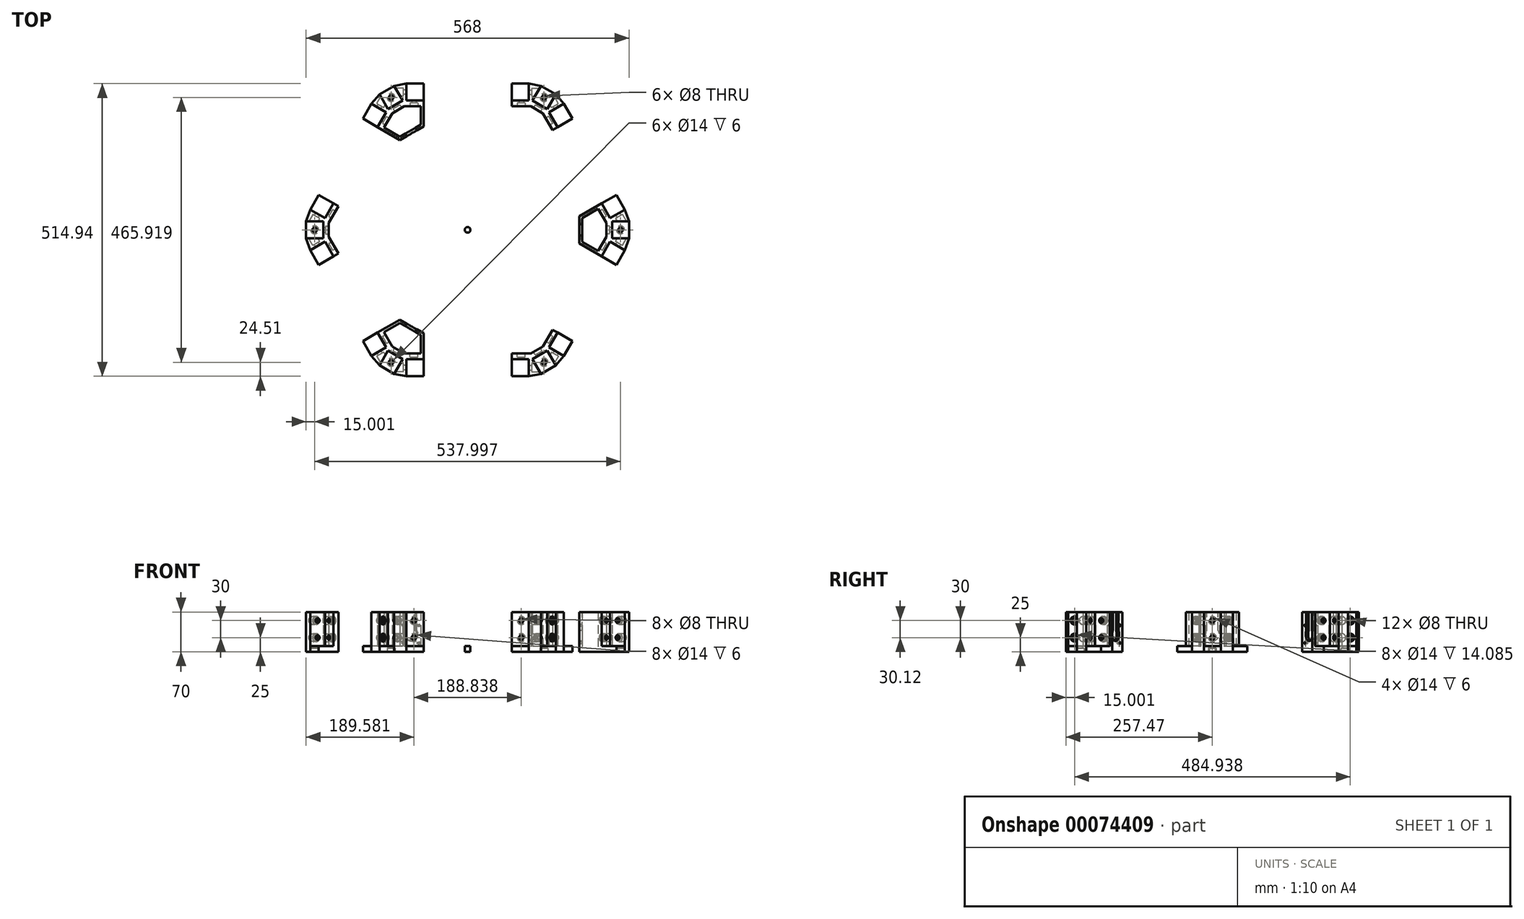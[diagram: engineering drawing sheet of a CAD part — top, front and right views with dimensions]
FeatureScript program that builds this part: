
annotation { "Feature Type Name" : "Feature", "Feature Type Description" : "" }
export const myFeature = defineFeature(function(context is Context, id is Id, definition is map)
    precondition{}
    {
        {
            var Q0;
            Q0=qCreatedBy(makeId("Top.planeOp"),FACE);
            var sketch = newSketch(context, id + "F0", { "sketchPlane" : qUnion([Q0])});
            skCircle(sketch, "E0", {"center": v(0, 0) * mm, "radius": 150 * mm, "construction": true});
            skCircle(sketch, "E1.cCircle", {"center": v(0, 0) * mm, "radius": 253.45 * mm, "construction": true});
            skLineSegment(sketch, "E1.0", {"start": v(-146.33, 253.45) * mm, "end": v(146.33, 253.45) * mm, "construction": true});
            skLineSegment(sketch, "E1.1", {"start": v(146.33, 253.45) * mm, "end": v(292.66, 0) * mm, "construction": true});
            skLineSegment(sketch, "E1.2", {"start": v(292.66, 0) * mm, "end": v(146.33, -253.45) * mm, "construction": true});
            skLineSegment(sketch, "E1.3", {"start": v(146.33, -253.45) * mm, "end": v(-146.33, -253.45) * mm, "construction": true});
            skLineSegment(sketch, "E1.4", {"start": v(-146.33, -253.45) * mm, "end": v(-292.66, 0) * mm, "construction": true});
            skLineSegment(sketch, "E1.5", {"start": v(-292.66, 0) * mm, "end": v(-146.33, 253.45) * mm, "construction": true});
            skPoint(sketch, "E1.0.midPoint", {"position": v(0, 253.45) * mm});
            skLineSegment(sketch, "E2", {"start": v(146.33, 253.45) * mm, "end": v(-146.33, -253.45) * mm, "construction": true});
            skCircle(sketch, "E3.cCircle", {"center": v(0, 0) * mm, "radius": 284 * mm, "construction": true});
            skLineSegment(sketch, "E3.0", {"start": v(0, 327.93) * mm, "end": v(284, 163.97) * mm, "construction": true});
            skLineSegment(sketch, "E3.1", {"start": v(284, 163.97) * mm, "end": v(284, -163.97) * mm, "construction": true});
            skLineSegment(sketch, "E3.2", {"start": v(284, -163.97) * mm, "end": v(0, -327.93) * mm, "construction": true});
            skLineSegment(sketch, "E3.3", {"start": v(0, -327.93) * mm, "end": v(-284, -163.97) * mm, "construction": true});
            skLineSegment(sketch, "E3.4", {"start": v(-284, -163.97) * mm, "end": v(-284, 163.97) * mm, "construction": true});
            skLineSegment(sketch, "E3.5", {"start": v(-284, 163.97) * mm, "end": v(0, 327.93) * mm, "construction": true});
            skPoint(sketch, "E3.0.midPoint", {"position": v(142, 245.95) * mm});
            skLineSegment(sketch, "E4", {"start": v(154.99, 238.45) * mm, "end": v(129, 253.45) * mm});
            skLineSegment(sketch, "E5", {"start": v(-154.99, 238.45) * mm, "end": v(-129, 253.45) * mm});
            skLineSegment(sketch, "E6", {"start": v(-129, 253.45) * mm, "end": v(-114, 227.47) * mm});
            skLineSegment(sketch, "E7", {"start": v(-114, 227.47) * mm, "end": v(-139.99, 212.47) * mm});
            skLineSegment(sketch, "E8", {"start": v(-139.99, 212.47) * mm, "end": v(-154.99, 238.45) * mm});
            skLineSegment(sketch, "E9", {"start": v(129, 253.45) * mm, "end": v(114, 227.47) * mm});
            skLineSegment(sketch, "E10", {"start": v(114, 227.47) * mm, "end": v(139.99, 212.47) * mm});
            skLineSegment(sketch, "E11", {"start": v(139.99, 212.47) * mm, "end": v(154.99, 238.45) * mm});
            skLineSegment(sketch, "E12", {"start": v(284, 15) * mm, "end": v(284, -15) * mm});
            skLineSegment(sketch, "E13", {"start": v(284, -15) * mm, "end": v(254, -15) * mm});
            skLineSegment(sketch, "E14", {"start": v(254, -15) * mm, "end": v(254, 15) * mm});
            skLineSegment(sketch, "E15", {"start": v(254, 15) * mm, "end": v(284, 15) * mm});
            skLineSegment(sketch, "E16", {"start": v(154.99, -238.45) * mm, "end": v(129, -253.45) * mm});
            skLineSegment(sketch, "E17", {"start": v(129, -253.45) * mm, "end": v(114, -227.47) * mm});
            skLineSegment(sketch, "E18", {"start": v(114, -227.47) * mm, "end": v(139.99, -212.47) * mm});
            skLineSegment(sketch, "E19", {"start": v(139.99, -212.47) * mm, "end": v(154.99, -238.45) * mm});
            skLineSegment(sketch, "E20", {"start": v(-129, -253.45) * mm, "end": v(-154.99, -238.45) * mm});
            skLineSegment(sketch, "E21", {"start": v(-154.99, -238.45) * mm, "end": v(-139.99, -212.47) * mm});
            skLineSegment(sketch, "E22", {"start": v(-139.99, -212.47) * mm, "end": v(-114, -227.47) * mm});
            skLineSegment(sketch, "E23", {"start": v(-114, -227.47) * mm, "end": v(-129, -253.45) * mm});
            skLineSegment(sketch, "E24", {"start": v(-284, -15) * mm, "end": v(-284, 15) * mm});
            skLineSegment(sketch, "E25", {"start": v(-284, 15) * mm, "end": v(-254, 15) * mm});
            skLineSegment(sketch, "E26", {"start": v(-254, 15) * mm, "end": v(-254, -15) * mm});
            skLineSegment(sketch, "E27", {"start": v(-254, -15) * mm, "end": v(-284, -15) * mm});
            skLineSegment(sketch, "E28", {"start": v(-254, 15) * mm, "end": v(-139.99, 212.47) * mm, "construction": true});
            skLineSegment(sketch, "E29", {"start": v(-254, -15) * mm, "end": v(-139.99, -212.47) * mm, "construction": true});
            skLineSegment(sketch, "E30", {"start": v(-114, -227.47) * mm, "end": v(114, -227.47) * mm, "construction": true});
            skLineSegment(sketch, "E31", {"start": v(139.99, -212.47) * mm, "end": v(254, -15) * mm, "construction": true});
            skLineSegment(sketch, "E32", {"start": v(254, 15) * mm, "end": v(139.99, 212.47) * mm, "construction": true});
            skLineSegment(sketch, "E33", {"start": v(114, 227.47) * mm, "end": v(-114, 227.47) * mm, "construction": true});
            skLineSegment(sketch, "E34", {"start": v(-114, 227.47) * mm, "end": v(-107.5, 227.47) * mm, "construction": true});
            skLineSegment(sketch, "E35", {"start": v(-107.5, 227.47) * mm, "end": v(-77.5, 227.47) * mm});
            skLineSegment(sketch, "E36", {"start": v(-77.5, 227.47) * mm, "end": v(-77.5, 217.47) * mm});
            skLineSegment(sketch, "E37", {"start": v(-77.5, 217.47) * mm, "end": v(-111.33, 217.47) * mm});
            skLineSegment(sketch, "E38", {"start": v(-111.33, 217.47) * mm, "end": v(-132.67, 205.15) * mm});
            skLineSegment(sketch, "E39", {"start": v(-132.67, 205.15) * mm, "end": v(-149.58, 175.86) * mm});
            skLineSegment(sketch, "E40", {"start": v(-149.58, 175.86) * mm, "end": v(-158.24, 180.86) * mm});
            skLineSegment(sketch, "E41", {"start": v(-158.24, 180.86) * mm, "end": v(-143.24, 206.84) * mm});
            skLineSegment(sketch, "E42", {"start": v(-143.24, 206.84) * mm, "end": v(-139.99, 212.47) * mm, "construction": true});
            skLineSegment(sketch, "E43", {"start": v(-154.99, 238.45) * mm, "end": v(-114, 227.47) * mm, "construction": true});
            skLineSegment(sketch, "E44", {"start": v(-129, 253.45) * mm, "end": v(-139.99, 212.47) * mm, "construction": true});
            skPoint(sketch, "E45", {"position": v(-134.5, 232.96) * mm});
            skCircle(sketch, "E46", {"center": v(0, 0) * mm, "radius": 5 * mm});
            skLineSegment(sketch, "E47", {"start": v(-118.15, 234.63) * mm, "end": v(-118.15, 248.63) * mm, "construction": true});
            skLineSegment(sketch, "E48.0", {"start": v(-112.15, 234.63) * mm, "end": v(-112.15, 248.63) * mm, "construction": true});
            skLineSegment(sketch, "E49.0", {"start": v(-107.5, 257.47) * mm, "end": v(-77.5, 257.47) * mm});
            skLineSegment(sketch, "E50.0", {"start": v(-184.22, 195.86) * mm, "end": v(-169.22, 221.84) * mm});
            skLineSegment(sketch, "E51", {"start": v(-154.99, 238.45) * mm, "end": v(-169.22, 221.84) * mm});
            skLineSegment(sketch, "E52", {"start": v(-107.5, 257.47) * mm, "end": v(-129, 253.45) * mm});
            skLineSegment(sketch, "E53", {"start": v(-107.5, 227.47) * mm, "end": v(-107.5, 257.47) * mm});
            skLineSegment(sketch, "E54", {"start": v(-77.5, 257.47) * mm, "end": v(-77.5, 227.47) * mm});
            skLineSegment(sketch, "E55", {"start": v(-158.24, 180.86) * mm, "end": v(-184.22, 195.86) * mm});
            skLineSegment(sketch, "E56", {"start": v(-143.24, 206.84) * mm, "end": v(-169.22, 221.84) * mm});
            skLineSegment(sketch, "E57", {"start": v(-107.5, 242.47) * mm, "end": v(-122.67, 242.47) * mm, "construction": true});
            skLineSegment(sketch, "E58", {"start": v(-149.58, 175.86) * mm, "end": v(-118.88, 158.14) * mm});
            skLineSegment(sketch, "E59", {"start": v(-118.88, 158.14) * mm, "end": v(-77.5, 182.02) * mm});
            skLineSegment(sketch, "E60", {"start": v(-77.5, 182.02) * mm, "end": v(-77.5, 217.47) * mm});
            skLineSegment(sketch, "E61", {"start": v(-122, 211.3) * mm, "end": v(-98.2, 170.08) * mm, "construction": true});
            skLineSegment(sketch, "E62.1", {"start": v(-118.88, 163.9) * mm, "end": v(-82.5, 184.9) * mm});
            skLineSegment(sketch, "E62.2", {"start": v(-147.08, 180.19) * mm, "end": v(-118.88, 163.9) * mm});
            skLineSegment(sketch, "E63", {"start": v(-82.5, 184.9) * mm, "end": v(-82.5, 217.47) * mm});
            skSolve(sketch);
        }
        {
            var Q0;
            Q0=makeQuery(id+"F0.imprint","IMPRINT",FACE,{"disambiguationData":[TD([[makeQuery(id+"F0.imprint","IMPRINT",EDGE,{"derivedFrom":sQuery(id+"F0.wireOp",EDGE,"E6")}),1.0]])]});
            var Q1;
            Q1=makeQuery(id+"F0.imprint","IMPRINT",FACE,{"disambiguationData":[TD([[makeQuery(id+"F0.imprint","IMPRINT",EDGE,{"derivedFrom":sQuery(id+"F0.wireOp",EDGE,"E25")}),1.0]])]});
            extrude(context, id + "F1", {"entities" : qUnion([Q0, Q1]), "depth" : 70 * mm});
        }
        {
            var Q0;
            Q0=makeQuery(id+"F0.imprint","IMPRINT",FACE,{"disambiguationData":[TD([[makeQuery(id+"F0.imprint","IMPRINT",EDGE,{"derivedFrom":sQuery(id+"F0.wireOp",EDGE,"gfhvg1Dc-7iLy-Ra7s-P4iO-IVNU9nK08UEl")}),-1.0]])]});
            var Q1;
            Q1=makeQuery(id+"F0.imprint","IMPRINT",FACE,{"disambiguationData":[TD([[makeQuery(id+"F0.imprint","IMPRINT",EDGE,{"derivedFrom":sQuery(id+"F0.wireOp",EDGE,"E5")}),-1.0]])]});
            var Q2;
            Q2=makeQuery(id+"F0.imprint","IMPRINT",FACE,{"disambiguationData":[TD([[makeQuery(id+"F0.imprint","IMPRINT",EDGE,{"derivedFrom":sQuery(id+"F0.wireOp",EDGE,"E41")}),1.0]])]});
            var Q3;
            Q3=makeQuery(id+"F0.imprint","IMPRINT",FACE,{"disambiguationData":[TD([[makeQuery(id+"F0.imprint","IMPRINT",EDGE,{"derivedFrom":sQuery(id+"F0.wireOp",EDGE,"kg992uxK-LLUE-ufWO-S31q-0ohrqG9XmHnS")}),1.0]])]});
            var Q4;
            Q4=makeQuery(id+"F0.imprint","IMPRINT",FACE,{"disambiguationData":[TD([[makeQuery(id+"F0.imprint","IMPRINT",EDGE,{"derivedFrom":sQuery(id+"F0.wireOp",EDGE,"zyB05oXD-GM3K-m8Ih-r1cb-nkl0ugIBj9Wl")}),1.0]])]});
            var Q5;
            Q5=makeQuery(id+"F0.imprint","IMPRINT",FACE,{"disambiguationData":[TD([[makeQuery(id+"F0.imprint","IMPRINT",EDGE,{"derivedFrom":sQuery(id+"F0.wireOp",EDGE,"ZcA5kg2R-B5n5-RwAf-hmlT-K68Li3uCES3B")}),-1.0]])]});
            var Q6;
            Q6=makeQuery(id+"F0.imprint","IMPRINT",FACE,{"disambiguationData":[TD([[makeQuery(id+"F0.imprint","IMPRINT",EDGE,{"derivedFrom":sQuery(id+"F0.wireOp",EDGE,"E46")}),1.0]])]});
            var Q7;
            Q7=makeQuery(id+"F0.imprint","IMPRINT",FACE,{"disambiguationData":[TD([[makeQuery(id+"F0.imprint","IMPRINT",EDGE,{"derivedFrom":sQuery(id+"F0.wireOp",EDGE,"E35")}),1.0]])]});
            extrude(context, id + "F2", {"entities" : qUnion([Q0, Q1, Q2, Q3, Q4, Q5, Q6, Q7]), "operationType" : NewBodyOperationType.ADD, "depth" : 10 * mm});
        }
        {
            var Q0;
            Q0=makeQuery(id+"F1.opExtrude","SWEPT_FACE",FACE,{"disambiguationData":[OSD([sQuery(id+"F0.wireOp",EDGE,"E53")])]});
            var Q1;
            Q1=makeQuery(id+"F1.opExtrude","CAP_VERTEX",VERTEX,{"disambiguationData":[OSD([sQuery(id+"F0.wireOp",EDGE,"E5"),sQuery(id+"F0.wireOp",EDGE,"E6"),sQuery(id+"F0.wireOp",EDGE,"E52")])],"isStart":false});
            cPlane(context, id + "F3", {"entities" : qUnion([Q0, Q1]), "cplaneType" : CPlaneType.PLANE_POINT, "offset" : 150 * mm, "width" : 150 * mm, "height" : 150 * mm});
        }
        {
            var Q0;
            Q0=qCreatedBy(id+"F3.planeOp",FACE);
            var sketch = newSketch(context, id + "F4", { "sketchPlane" : qUnion([Q0])});
            skLineSegment(sketch, "E64.0", {"start": v(242.47, 70.12) * mm, "end": v(242.47, 10) * mm, "construction": true});
            skPoint(sketch, "E65", {"position": v(242.47, 55.12) * mm});
            skPoint(sketch, "E66", {"position": v(242.47, 25) * mm});
            skSolve(sketch);
        }
        {
            var Q0;
            Q0=makeQuery(id+"F1.opExtrude","SWEPT_FACE",FACE,{"disambiguationData":[OSD([sQuery(id+"F0.wireOp",EDGE,"E56")])]});
            var Q1;
            Q1=makeQuery(id+"F1.opExtrude","CAP_VERTEX",VERTEX,{"disambiguationData":[OSD([sQuery(id+"F0.wireOp",EDGE,"E5"),sQuery(id+"F0.wireOp",EDGE,"E8"),sQuery(id+"F0.wireOp",EDGE,"E51")])],"isStart":false});
            cPlane(context, id + "F5", {"entities" : qUnion([Q0, Q1]), "cplaneType" : CPlaneType.PLANE_POINT, "offset" : 150 * mm, "width" : 150 * mm, "height" : 150 * mm});
        }
        {
            var Q0;
            Q0=qCreatedBy(id+"F5.planeOp",FACE);
            var sketch = newSketch(context, id + "F6", { "sketchPlane" : qUnion([Q0])});
            skLineSegment(sketch, "E67.0", {"start": v(-242.47, 70) * mm, "end": v(-242.47, 10) * mm, "construction": true});
            skPoint(sketch, "E68", {"position": v(-242.47, 55) * mm});
            skPoint(sketch, "E69", {"position": v(-242.47, 25) * mm});
            skSolve(sketch);
        }
        {
            var Q0;
            Q0=makeQuery(id+"F1.opExtrude","SWEPT_FACE",FACE,{"disambiguationData":[OSD([sQuery(id+"F0.wireOp",EDGE,"E38")])]});
            var sketch = newSketch(context, id + "F7", { "sketchPlane" : qUnion([Q0])});
            skLineSegment(sketch, "E70", {"start": v(0, 70) * mm, "end": v(0, 0) * mm, "construction": true});
            skPoint(sketch, "E71", {"position": v(0, 55) * mm});
            skPoint(sketch, "E72", {"position": v(0, 25) * mm});
            skSolve(sketch);
        }
        {
            var Q0;
            Q0=makeQuery(id+"F1.opExtrude","SWEPT_FACE",FACE,{"disambiguationData":[OSD([sQuery(id+"F0.wireOp",EDGE,"E39")])]});
            var sketch = newSketch(context, id + "F8", { "sketchPlane" : qUnion([Q0])});
            skLineSegment(sketch, "E73", {"start": v(94.42, 70) * mm, "end": v(94.42, 0) * mm, "construction": true});
            skPoint(sketch, "E74", {"position": v(94.42, 55) * mm});
            skPoint(sketch, "E75", {"position": v(94.42, 25) * mm});
            skSolve(sketch);
        }
        {
            var Q0;
            Q0=makeQuery(id+"F1.opExtrude","SWEPT_FACE",FACE,{"disambiguationData":[OSD([sQuery(id+"F0.wireOp",EDGE,"E37")])]});
            var sketch = newSketch(context, id + "F9", { "sketchPlane" : qUnion([Q0])});
            skLineSegment(sketch, "E76", {"start": v(-94.42, 70) * mm, "end": v(-94.42, 0) * mm, "construction": true});
            skPoint(sketch, "E77", {"position": v(-94.42, 55) * mm});
            skPoint(sketch, "E78", {"position": v(-94.42, 25) * mm});
            skSolve(sketch);
        }
        {
            var Q0;
            Q0=sQuery(id+"F4.wireOp",VERTEX,"E65");
            var Q1;
            Q1=sQuery(id+"F4.wireOp",VERTEX,"E66");
            var Q2;
            Q2=sQuery(id+"F0.wireOp",VERTEX,"E45");
            var Q3;
            Q3=sQuery(id+"F6.wireOp",VERTEX,"cff155ce-5f81-47e9-b263-279717c5aa05");
            var Q4;
            Q4=sQuery(id+"F6.wireOp",VERTEX,"238236e4-252f-4cb6-8429-7a6d3b7dbdbb");
            var Q5;
            Q5=sQuery(id+"F6.wireOp",VERTEX,"E68");
            var Q6;
            Q6=sQuery(id+"F6.wireOp",VERTEX,"E69");
            var Q7;
            Q7=makeQuery(id+"F1.opExtrude","SWEPT_BODY",BODY,{"disambiguationData":[OSD([sQuery(id+"F0.wireOp",EDGE,"E6"),sQuery(id+"F0.wireOp",EDGE,"E7"),sQuery(id+"F0.wireOp",EDGE,"E8"),sQuery(id+"F0.wireOp",EDGE,"gfhvg1Dc-7iLy-Ra7s-P4iO-IVNU9nK08UEl"),sQuery(id+"F0.wireOp",EDGE,"2Ei9XriT-fD9c-ETMH-U4qR-QOi2l2HyO4ls"),sQuery(id+"F0.wireOp",EDGE,"E35"),sQuery(id+"F0.wireOp",EDGE,"E36"),sQuery(id+"F0.wireOp",EDGE,"E37"),sQuery(id+"F0.wireOp",EDGE,"E38"),sQuery(id+"F0.wireOp",EDGE,"E39"),sQuery(id+"F0.wireOp",EDGE,"E40"),sQuery(id+"F0.wireOp",EDGE,"E41"),sQuery(id+"F0.wireOp",EDGE,"uSjWHJkC-35aW-f7bu-jVbw-ONZoDCyZtA0Y"),sQuery(id+"F0.wireOp",EDGE,"6PwrACHb-G9Z9-2ubd-gtxy-jkFo4IrFMrrZ")])]});
            hole(context, id + "F10", {"style" : HoleStyle.C_BORE, "holeDiameter" : 8 * mm, "cBoreDiameter" : 14 * mm, "cBoreDepth" : 6 * mm, "endStyle" : HoleEndStyle.BLIND, "oppositeDirection" : true, "holeDepth" : 20 * mm, "locations" : qUnion([Q0, Q1, Q2, Q3, Q4, Q5, Q6]), "scope" : qUnion([Q7])});
        }
        {
            var Q0;
            Q0=sQuery(id+"F9.wireOp",VERTEX,"E77");
            var Q1;
            Q1=sQuery(id+"F9.wireOp",VERTEX,"E78");
            var Q2;
            Q2=sQuery(id+"F7.wireOp",VERTEX,"E71");
            var Q3;
            Q3=sQuery(id+"F7.wireOp",VERTEX,"E72");
            var Q4;
            Q4=sQuery(id+"F8.wireOp",VERTEX,"E75");
            var Q5;
            Q5=sQuery(id+"F8.wireOp",VERTEX,"E74");
            var Q6;
            Q6=makeQuery(id+"F1.opExtrude","SWEPT_BODY",BODY,{"disambiguationData":[OSD([sQuery(id+"F0.wireOp",EDGE,"E6"),sQuery(id+"F0.wireOp",EDGE,"E7"),sQuery(id+"F0.wireOp",EDGE,"E8"),sQuery(id+"F0.wireOp",EDGE,"gfhvg1Dc-7iLy-Ra7s-P4iO-IVNU9nK08UEl"),sQuery(id+"F0.wireOp",EDGE,"2Ei9XriT-fD9c-ETMH-U4qR-QOi2l2HyO4ls"),sQuery(id+"F0.wireOp",EDGE,"E35"),sQuery(id+"F0.wireOp",EDGE,"E36"),sQuery(id+"F0.wireOp",EDGE,"E37"),sQuery(id+"F0.wireOp",EDGE,"E38"),sQuery(id+"F0.wireOp",EDGE,"E39"),sQuery(id+"F0.wireOp",EDGE,"E40"),sQuery(id+"F0.wireOp",EDGE,"E41"),sQuery(id+"F0.wireOp",EDGE,"uSjWHJkC-35aW-f7bu-jVbw-ONZoDCyZtA0Y"),sQuery(id+"F0.wireOp",EDGE,"6PwrACHb-G9Z9-2ubd-gtxy-jkFo4IrFMrrZ")])]});
            hole(context, id + "F11", {"style" : HoleStyle.C_BORE, "holeDiameter" : 8 * mm, "cBoreDiameter" : 14 * mm, "cBoreDepth" : 6 * mm, "endStyle" : HoleEndStyle.THROUGH, "locations" : qUnion([Q0, Q1, Q2, Q3, Q4, Q5]), "scope" : qUnion([Q6])});
        }
        {
            var Q0;
            Q0=makeQuery(id+"F1.opExtrude","SWEPT_BODY",BODY,{"disambiguationData":[OSD([sQuery(id+"F0.wireOp",EDGE,"E6"),sQuery(id+"F0.wireOp",EDGE,"E7"),sQuery(id+"F0.wireOp",EDGE,"E8"),sQuery(id+"F0.wireOp",EDGE,"gfhvg1Dc-7iLy-Ra7s-P4iO-IVNU9nK08UEl"),sQuery(id+"F0.wireOp",EDGE,"2Ei9XriT-fD9c-ETMH-U4qR-QOi2l2HyO4ls"),sQuery(id+"F0.wireOp",EDGE,"E35"),sQuery(id+"F0.wireOp",EDGE,"E36"),sQuery(id+"F0.wireOp",EDGE,"E37"),sQuery(id+"F0.wireOp",EDGE,"E38"),sQuery(id+"F0.wireOp",EDGE,"E39"),sQuery(id+"F0.wireOp",EDGE,"E40"),sQuery(id+"F0.wireOp",EDGE,"E41"),sQuery(id+"F0.wireOp",EDGE,"uSjWHJkC-35aW-f7bu-jVbw-ONZoDCyZtA0Y"),sQuery(id+"F0.wireOp",EDGE,"6PwrACHb-G9Z9-2ubd-gtxy-jkFo4IrFMrrZ")])]});
            var Q1;
            Q1=sQuery(id+"F0.wireOp",EDGE,"E3.cCircle");
            circularPattern(context, id + "F12", {"entities" : qUnion([Q0]), "axis" : qUnion([Q1]), "angle" : 60 * degree, "instanceCount" : 2});
        }
        {
            var Q0;
            {var subQ0=sQuery(id+"F0.wireOp",EDGE,"E58");Q0=makeQuery(id+"F0.imprint","IMPRINT",FACE,{"disambiguationData":[TD([[makeQuery(id+"F0.imprint","IMPRINT",EDGE,{"derivedFrom":subQ0}),1.0]])]});}
            extrude(context, id + "F13", {"entities" : qUnion([Q0]), "operationType" : NewBodyOperationType.ADD, "depth" : 70 * mm});
        }
        {
            var Q0;
            Q0=makeQuery(id+"F13.opExtrude","SWEPT_FACE",FACE,{"disambiguationData":[OSD([sQuery(id+"F0.wireOp",EDGE,"E59")])]});
            var sketch = newSketch(context, id + "F14", { "sketchPlane" : qUnion([Q0])});
            skLineSegment(sketch, "E79.0", {"start": v(-23.89, 10) * mm, "end": v(23.89, 10) * mm, "construction": true});
            skLineSegment(sketch, "E80.0", {"start": v(-23.89, 52) * mm, "end": v(23.89, 52) * mm, "construction": true});
            skLineSegment(sketch, "E81.0", {"start": v(-23.89, 46.5) * mm, "end": v(23.89, 46.5) * mm, "construction": true});
            skLineSegment(sketch, "E82.0", {"start": v(-23.89, 15.5) * mm, "end": v(23.89, 15.5) * mm, "construction": true});
            skPoint(sketch, "E83", {"position": v(0, 31) * mm});
            skLineSegment(sketch, "E84", {"start": v(0, 70) * mm, "end": v(0, 0) * mm, "construction": true});
            skLineSegment(sketch, "E85.0", {"start": v(-15.5, 70) * mm, "end": v(-15.5, 0) * mm, "construction": true});
            skLineSegment(sketch, "E86.0", {"start": v(15.5, 70) * mm, "end": v(15.5, 0) * mm, "construction": true});
            skLineSegment(sketch, "E87", {"start": v(15.5, 15.5) * mm, "end": v(-15.5, 46.5) * mm, "construction": true});
            skLineSegment(sketch, "E88", {"start": v(15.5, 46.5) * mm, "end": v(-15.5, 15.5) * mm, "construction": true});
            skCircle(sketch, "E89", {"center": v(0, 31) * mm, "radius": 12 * mm});
            skLineSegment(sketch, "E90.0", {"start": v(-10, 70) * mm, "end": v(-10, 0) * mm, "construction": true});
            skLineSegment(sketch, "E91.0", {"start": v(10, 70) * mm, "end": v(10, 0) * mm, "construction": true});
            skLineSegment(sketch, "E92", {"start": v(-10, 37.63) * mm, "end": v(-10, 70) * mm});
            skLineSegment(sketch, "E93", {"start": v(10, 37.63) * mm, "end": v(10, 70) * mm});
            skSolve(sketch);
        }
        {
            var Q0;
            Q0 = qSketchRegion(id + "F14", true);
            var Q1;
            {var subQ0=sQuery(id+"F14.wireOp",EDGE,"E92");Q1=makeQuery(id+"F14.imprint","IMPRINT",FACE,{"disambiguationData":[TD([[makeQuery(id+"F14.imprint","IMPRINT",EDGE,{"derivedFrom":subQ0}),-1.0]])]});}
            extrude(context, id + "F15", {"entities" : qUnion([Q0, Q1]), "operationType" : NewBodyOperationType.REMOVE, "oppositeDirection" : true, "depth" : 5 * mm});
        }
        {
            var Q0;
            Q0=sQuery(id+"F14.wireOp",VERTEX,"E87.end");
            var Q1;
            Q1=sQuery(id+"F14.wireOp",VERTEX,"E88.start");
            var Q2;
            Q2=sQuery(id+"F14.wireOp",VERTEX,"E87.start");
            var Q3;
            Q3=sQuery(id+"F14.wireOp",VERTEX,"E88.end");
            var Q4;
            Q4=makeQuery(id+"F1.opExtrude","SWEPT_BODY",BODY,{"disambiguationData":[OSD([sQuery(id+"F0.wireOp",EDGE,"E6"),sQuery(id+"F0.wireOp",EDGE,"E7"),sQuery(id+"F0.wireOp",EDGE,"E8"),sQuery(id+"F0.wireOp",EDGE,"E35"),sQuery(id+"F0.wireOp",EDGE,"E36"),sQuery(id+"F0.wireOp",EDGE,"E37"),sQuery(id+"F0.wireOp",EDGE,"E38"),sQuery(id+"F0.wireOp",EDGE,"E39"),sQuery(id+"F0.wireOp",EDGE,"E40"),sQuery(id+"F0.wireOp",EDGE,"E41"),sQuery(id+"F0.wireOp",EDGE,"E51"),sQuery(id+"F0.wireOp",EDGE,"E52"),sQuery(id+"F0.wireOp",EDGE,"E53"),sQuery(id+"F0.wireOp",EDGE,"E56")])]});
            hole(context, id + "F16", {"style" : HoleStyle.SIMPLE, "holeDiameter" : 3 * mm, "endStyle" : HoleEndStyle.BLIND, "holeDepth" : 20 * mm, "locations" : qUnion([Q0, Q1, Q2, Q3]), "scope" : qUnion([Q4])});
        }
        {
            var Q0;
            Q0=makeQuery(id+"F1.opExtrude","SWEPT_BODY",BODY,{"disambiguationData":[OSD([sQuery(id+"F0.wireOp",EDGE,"E6"),sQuery(id+"F0.wireOp",EDGE,"E7"),sQuery(id+"F0.wireOp",EDGE,"E8"),sQuery(id+"F0.wireOp",EDGE,"gfhvg1Dc-7iLy-Ra7s-P4iO-IVNU9nK08UEl"),sQuery(id+"F0.wireOp",EDGE,"2Ei9XriT-fD9c-ETMH-U4qR-QOi2l2HyO4ls"),sQuery(id+"F0.wireOp",EDGE,"E35"),sQuery(id+"F0.wireOp",EDGE,"E36"),sQuery(id+"F0.wireOp",EDGE,"E37"),sQuery(id+"F0.wireOp",EDGE,"E38"),sQuery(id+"F0.wireOp",EDGE,"E39"),sQuery(id+"F0.wireOp",EDGE,"E40"),sQuery(id+"F0.wireOp",EDGE,"E41"),sQuery(id+"F0.wireOp",EDGE,"uSjWHJkC-35aW-f7bu-jVbw-ONZoDCyZtA0Y"),sQuery(id+"F0.wireOp",EDGE,"6PwrACHb-G9Z9-2ubd-gtxy-jkFo4IrFMrrZ")])]});
            var Q1;
            Q1=sQuery(id+"F0.wireOp",EDGE,"E3.cCircle");
            circularPattern(context, id + "F17", {"entities" : qUnion([Q0]), "axis" : qUnion([Q1]), "angle" : 120 * degree, "instanceCount" : 3});
        }
        {
            var Q0;
            Q0=makeQuery(id+"F12.opPattern","COPY",BODY,{"derivedFrom":makeQuery(id+"F1.opExtrude","SWEPT_BODY",BODY,{"disambiguationData":[OSD([sQuery(id+"F0.wireOp",EDGE,"E6"),sQuery(id+"F0.wireOp",EDGE,"E7"),sQuery(id+"F0.wireOp",EDGE,"E8"),sQuery(id+"F0.wireOp",EDGE,"gfhvg1Dc-7iLy-Ra7s-P4iO-IVNU9nK08UEl"),sQuery(id+"F0.wireOp",EDGE,"2Ei9XriT-fD9c-ETMH-U4qR-QOi2l2HyO4ls"),sQuery(id+"F0.wireOp",EDGE,"E35"),sQuery(id+"F0.wireOp",EDGE,"E36"),sQuery(id+"F0.wireOp",EDGE,"E37"),sQuery(id+"F0.wireOp",EDGE,"E38"),sQuery(id+"F0.wireOp",EDGE,"E39"),sQuery(id+"F0.wireOp",EDGE,"E40"),sQuery(id+"F0.wireOp",EDGE,"E41"),sQuery(id+"F0.wireOp",EDGE,"uSjWHJkC-35aW-f7bu-jVbw-ONZoDCyZtA0Y"),sQuery(id+"F0.wireOp",EDGE,"6PwrACHb-G9Z9-2ubd-gtxy-jkFo4IrFMrrZ")])]}),"instanceName":"1"});
            var Q1;
            Q1=sQuery(id+"F0.wireOp",EDGE,"E3.cCircle");
            circularPattern(context, id + "F18", {"entities" : qUnion([Q0]), "axis" : qUnion([Q1]), "angle" : 120 * degree, "instanceCount" : 3});
        }
        {
            var Q0;
            Q0=makeQuery(id+"F15.boolean.opBoolean","COPY",EDGE,{"derivedFrom":makeQuery(id+"F15.opExtrude","SWEPT_EDGE",EDGE,{"disambiguationData":[OSD([sQuery(id+"F0.wireOp",EDGE,"E59"),sQuery(id+"F14.wireOp",EDGE,"E92")])]})});
            var Q1;
            Q1=makeQuery(id+"F15.boolean.opBoolean","COPY",EDGE,{"derivedFrom":makeQuery(id+"F15.opExtrude","SWEPT_EDGE",EDGE,{"disambiguationData":[OSD([sQuery(id+"F0.wireOp",EDGE,"E59"),sQuery(id+"F14.wireOp",EDGE,"E93")])]})});
            var Q2;
            Q2=makeQuery(id+"F15.boolean.opBoolean","COPY",EDGE,{"derivedFrom":makeQuery(id+"F15.opExtrude","SWEPT_EDGE",EDGE,{"disambiguationData":[OSD([sQuery(id+"F14.wireOp",EDGE,"E89"),sQuery(id+"F14.wireOp",EDGE,"E92")])]})});
            var Q3;
            Q3=makeQuery(id+"F15.boolean.opBoolean","COPY",EDGE,{"derivedFrom":makeQuery(id+"F15.opExtrude","SWEPT_EDGE",EDGE,{"disambiguationData":[OSD([sQuery(id+"F14.wireOp",EDGE,"E89"),sQuery(id+"F14.wireOp",EDGE,"E93")])]})});
            fillet(context, id + "F19", {"entities" : qUnion([Q0, Q1, Q2, Q3]), "radius" : 10 * mm, "tangentPropagation" : true, "allowEdgeOverflow" : false});
        }
    });
